# Revit family: Electronics_Commercial-Audio_Biamp_Paging-Station_MICPAT-2_MICPAT-4_MICPAT-D
name_source: partatom
category: Communication Devices
units: mm (PartAtom-declared; Revit-internal decimal feet)

## family parameters
Cut with Voids When Loaded = No
Host = Face
Maintain Annotation Orientation = No
OmniClass Number = 23.85.10.11.14.14.11
Part Type = Normal
Room Calculation Point = No
Round Connector Dimension = Use Diameter
Shared = No

## types (3) — shared parameters
Apparent Load = 0 VA
Default Elevation = 4' - 0"
Manufacturer = Biamp
Max Power Consumption = 0 W
Number of Poles = 1
Power Factor = 1
Product Documentation Link = https://downloads.biamp.com
Product Page URL = https://www.biamp.com
Product data url = https://www.bimobject.com
URL = https://www.biamp.com

## per-type parameters (varying)
| type | Active | Buttons | Cable lenght in m | Cable type | Connector Description | Depth | Description | Frequency range | Height | Housing Material | Indicator | MICPAT-2 | MICPAT-2-D | MICPAT-4 | MICPAT-D | Polar pattern | Power type | Rated output impedance  in ohms | Voltage | Weight | Width | Zones |
| MICPAT-2 |  | 2 push to-talk | 5 | 2 core + 2 core screened | Open wire | 0' - 7" | MICPAT-2 Selective 2-Zone Paging Station | 80 Hz - 12 kHz | 0' - 2" | Biamp - Plastic - Black | 1 per button | Yes | Yes | No | No | Uni-directional |  | 600 balanced | 0.275 V | 1.87 lb | 0' - 5" | 2 |
| MICPAT-D |  | Toggle switch : talk - off - continuous talk | 3 |  | DIN5 | 0' - 6 1/2" | MICPAT-D All Call Dynamic Paging Microphone | 80 Hz - 12 kHz | 0' - 2" | Biamp - Plastic - Black |  | No | Yes | No | Yes | Uni-directional |  | 600 | 0.005 V | 1.79 lb | 0' - 4 1/2" |  |
| MICPAT-4 | Yes | 4 selection + Call + All Call | 5 | CAT5 | RJ45 | 0' - 6 1/2" | MICPAT-4 Selective 4-Zone Paging Station | 80 Hz - 20 kHz | 0' - 2 1/2" | Biamp - Plastic - Gray | 1 per button + multi color status | No | No | Yes | No | directional, low feedback, electret capsule | Phantom | 50 balanced | 0.000 V | 1.21 lb | 0' - 4 1/2" | 4 |

note: column(s) folded — value = type name in every type: Model

## geometry (parser evidence)
native form markers: Sweep x3
no freeform markers — native parametric forms only
